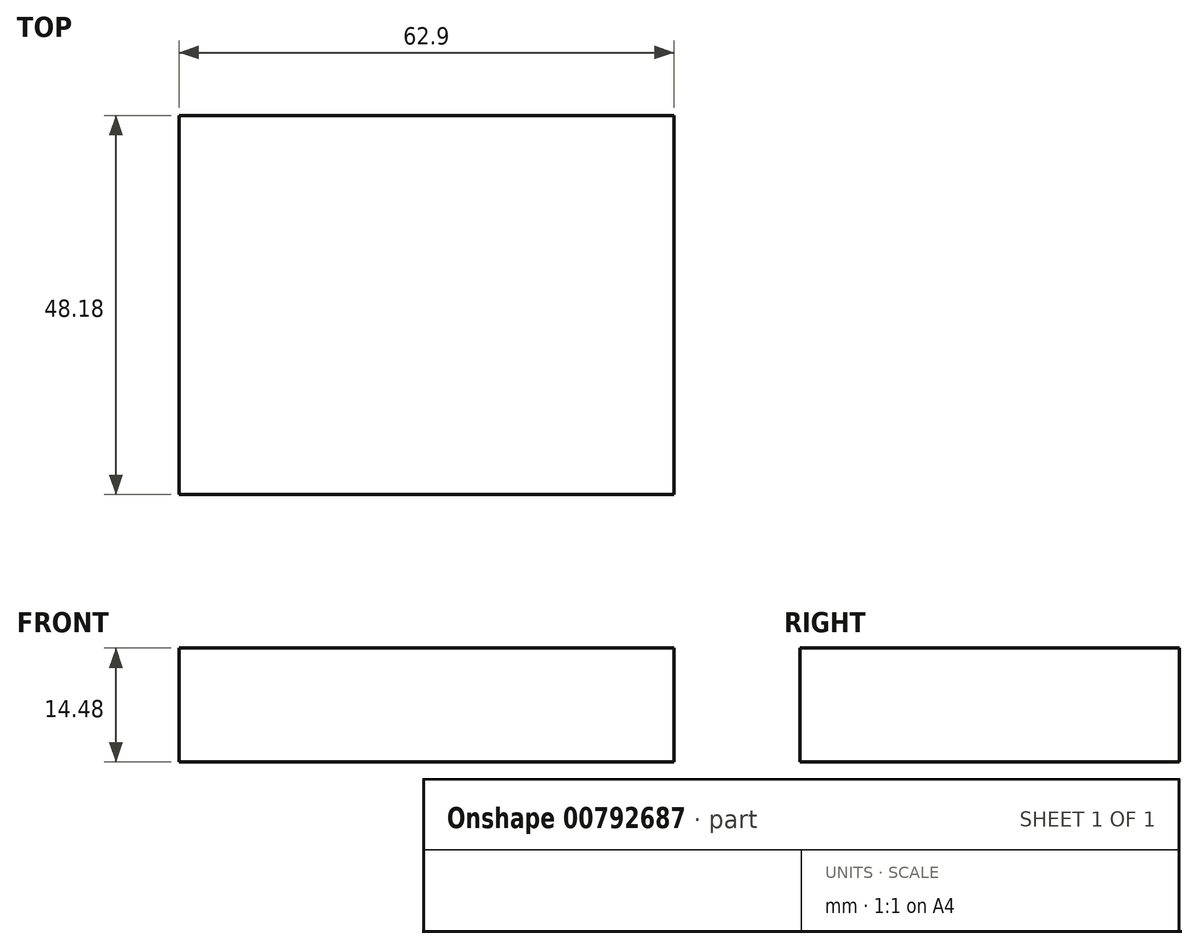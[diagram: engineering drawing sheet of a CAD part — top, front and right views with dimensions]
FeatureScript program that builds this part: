
annotation { "Feature Type Name" : "Feature", "Feature Type Description" : "" }
export const myFeature = defineFeature(function(context is Context, id is Id, definition is map)
    precondition{}
    {
        {
            var Q0;
            Q0=qCreatedBy(makeId("Top.planeOp"),FACE);
            var sketch = newSketch(context, id + "F0", { "sketchPlane" : qUnion([Q0])});
            skLineSegment(sketch, "E0.bottom", {"start": v(-137.06, 0) * mm, "end": v(-74.16, 0) * mm});
            skLineSegment(sketch, "E0.top", {"start": v(-137.06, -48.18) * mm, "end": v(-74.16, -48.18) * mm});
            skLineSegment(sketch, "E0.left", {"start": v(-137.06, 0) * mm, "end": v(-137.06, -48.18) * mm});
            skLineSegment(sketch, "E0.right", {"start": v(-74.16, 0) * mm, "end": v(-74.16, -48.18) * mm});
            skSolve(sketch);
        }
        {
            var Q0;
            Q0=makeQuery(id+"F0.imprint","IMPRINT",FACE,{"disambiguationData":[TD([[makeQuery(id+"F0.imprint","IMPRINT",EDGE,{"derivedFrom":sQuery(id+"F0.wireOp",EDGE,"E0.bottom")}),-1.0]])]});
            extrude(context, id + "F1", {"entities" : qUnion([Q0]), "depth" : 14.48 * mm, "offsetDistance" : 25.4 * mm});
        }
    });
